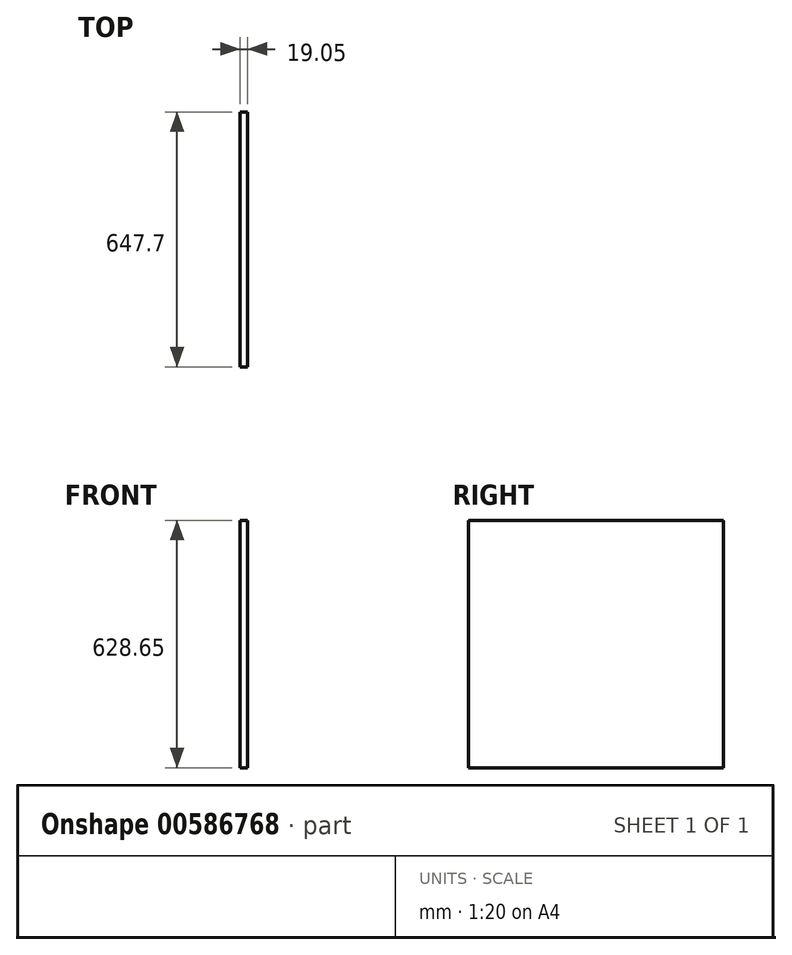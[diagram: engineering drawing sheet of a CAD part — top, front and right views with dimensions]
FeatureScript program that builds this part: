
annotation { "Feature Type Name" : "Feature", "Feature Type Description" : "" }
export const myFeature = defineFeature(function(context is Context, id is Id, definition is map)
    precondition{}
    {
        {
            var Q0;
            Q0=qCreatedBy(makeId("Right.planeOp"),FACE);
            var sketch = newSketch(context, id + "F0", { "sketchPlane" : qUnion([Q0])});
            skLineSegment(sketch, "E0.bottom", {"start": v(-411.87, 296.56) * mm, "end": v(235.83, 296.56) * mm});
            skLineSegment(sketch, "E0.top", {"start": v(-411.87, -332.1) * mm, "end": v(235.83, -332.1) * mm});
            skLineSegment(sketch, "E0.left", {"start": v(-411.87, 296.56) * mm, "end": v(-411.87, -332.1) * mm});
            skLineSegment(sketch, "E0.right", {"start": v(235.83, 296.56) * mm, "end": v(235.83, -332.1) * mm});
            skSolve(sketch);
        }
        {
            var Q0;
            Q0 = qSketchRegion(id + "F0", true);
            extrude(context, id + "F1", {"entities" : qUnion([Q0]), "depth" : 19.05 * mm, "offsetDistance" : 25.4 * mm});
        }
    });
